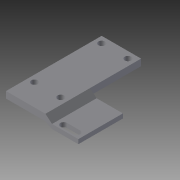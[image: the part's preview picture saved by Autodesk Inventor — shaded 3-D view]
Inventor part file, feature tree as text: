
AUTODESK INVENTOR PART (.ipt)
format: ipt  version: 2015 (Build 190159000, 159)  size: 348,672 bytes
history: native  units: in
note: dims shown in document units (in); Inventor stores cm internally (conversion verified against a paired STEP export)
features: sketch x29, extrude x27, plane x5, fillet x2, pattern_circular x1, mirror x1, sweep x1
ambient origin geometry x8: Origin, YZ Plane, XZ Plane, XY Plane, X Axis, Y Axis, Z Axis, Center Point
bodies: Solid1 (feature_tree)
feature tree (66):
  extrude  "Extrusion1"  Depth=0.1181in
  fillet  "Fillet1"  Radius=0.1969in
  fillet  "Fillet2"  [1 undecoded]
  plane  "Work Plane1"
  extrude  "Extrusion3"  Depth=0.1181in
  pattern_circular  "Circular Pattern1"  Count=4 Angle=360.0deg
  extrude  "Extrusion5"  Depth=0.1181in TaperAngle=0.0deg
  extrude  "Extrusion6"  Depth=0.1181in TaperAngle=0.0deg
  extrude  "Extrusion7"  Depth=0.3937in TaperAngle=0.0deg
  extrude  "Extrusion8"  Depth=3.937in TaperAngle=0.0deg
  extrude  "Extrusion9"  Depth=0.1181in TaperAngle=0.0deg
  extrude  "Extrusion10"  Depth=0.5512in
  extrude  "Extrusion11"  Depth=0.7087in
  extrude  "Extrusion12"  Depth=0.3937in
  extrude  "Extrusion13"  Depth=0.1181in TaperAngle=0.0deg
  extrude  "Extrusion14"  Depth=0.0106in TaperAngle=0.0deg
  extrude  "Extrusion16"  Depth=0.1181in TaperAngle=0.0deg
  extrude  "Extrusion17"  Depth=0.2953in
  extrude  "Extrusion18"  Depth=0.1181in
  extrude  "Extrusion19"  Depth=0.1181in
  extrude  "Extrusion21"  Depth=0.1181in
  extrude  "Extrusion22"  Depth=0.2953in TaperAngle=0.0deg
  extrude  "Extrusion23"  Depth=1.1811in TaperAngle=0.0deg
  extrude  "Extrusion24"  [1 undecoded]
  mirror  "Mirror1"
  plane  "Work Plane2"
  extrude  "Extrusion25"  Depth=0.1181in TaperAngle=0.0deg
  extrude  "Extrusion26"  Depth=0.1969in
  plane  "Work Plane3"
  plane  "Work Plane4"
  extrude  "Extrusion27"  Depth=0.1181in
  sketch  "Sketch44"  dims[d116=0.1969in d117=0.1969in]
  plane  "Work Plane7"
  sweep  "Sweep2"
  extrude  "Extrusion28"  TaperAngle=0.0deg  [1 undecoded]
  extrude  "Extrusion29"  Depth=0.7087in
  extrude  "Extrusion30"  Depth=0.0591in
  extrude  "Extrusion31"  Depth=0.0591in
  sketch  "Sketch1"  dims[d4=0.1181in d5=0.0in d6=0.1969in d7=0.1969in d8=-0.1969in]
  sketch  "Sketch6"  dims[d17=0.7087in d21=0.1181in]
  sketch  "Sketch8"  dims[d22=0.1181in]
  sketch  "Sketch9"  dims[d24=0.7087in d25=0.0in d26=1.5748in d27=360.0deg]
  sketch  "Sketch10"  dims[d35=0.1969in d36=0.1181in d37=0.0in]
  sketch  "Sketch12"  dims[d39=0.1969in d40=0.1181in d41=0.0in]
  sketch  "Sketch13"  dims[d42=0.3937in d43=0.0in d44=3.937in d45=0.0in]
  sketch  "Sketch14"  dims[d46=3.937in d47=0.0in d48=3.937in d49=0.0in]
  sketch  "Sketch17"  dims[d50=0.1181in d51=3.937in d52=0.0in]
  sketch  "Sketch18"  dims[d53=0.5118in d54=0.0in d55=0.5512in]
  sketch  "Sketch20"  dims[d56=0.126in d57=0.7087in]
  sketch  "Sketch22"  dims[d58=0.3937in d59=0.3937in]
  sketch  "Sketch24"  dims[d60=0.7087in d61=0.0in d62=0.1181in d63=0.0in]
  sketch  "Sketch25"  dims[d69=0.0118in d70=0.0in d71=0.0106in d72=0.0in]
  sketch  "Sketch26"  dims[d73=0.0012in d74=0.0in d75=0.1181in d76=0.0in]
  sketch  "Sketch27"  dims[d84=1.1811in d85=0.0in d86=0.2953in]
  sketch  "Sketch32"  dims[d87=0.7087in d88=0.0in d89=0.1181in]
  sketch  "Sketch33"  dims[d90=0.1181in d91=0.1181in]
  sketch  "Sketch34"  dims[d92=0.1181in d93=0.1181in]
  sketch  "Sketch35"  dims[d94=0.7087in d95=0.0in d96=0.2953in d97=0.0in]
  sketch  "Sketch38"  dims[d99=0.0in d100=1.1811in d101=0.0in]
  sketch  "Sketch39"  dims[d102=0.3937in d103=0.0in d106=-0.1575in]
  sketch  "Sketch43"  dims[d112=-0.5512in d114=0.1181in d115=0.0in]
  sketch  "Sketch45"  dims[d118=0.0591in d119=0.1181in]
  sketch  "Sketch46"  dims[d120=0.0591in d121=0.1181in]
  sketch  "Sketch47"  dims[d122=0.0591in d123=0.0in d124=0.0in]
  sketch  "Sketch48"  dims[d125=0.4724in d126=0.0in d127=0.7087in]
  sketch  "Sketch49"  dims[d128=0.3543in d129=0.0591in d130=0.2362in d131=0.4724in d132=0.0in d133=0.0394in d134=0.0in d135=0.9843in d136=0.0in]
note: 3 required parameter values undecoded (feature->parameter linkage not recoverable at this tier; creation-order binding heuristic only, values carry confidence <= 0.55)
